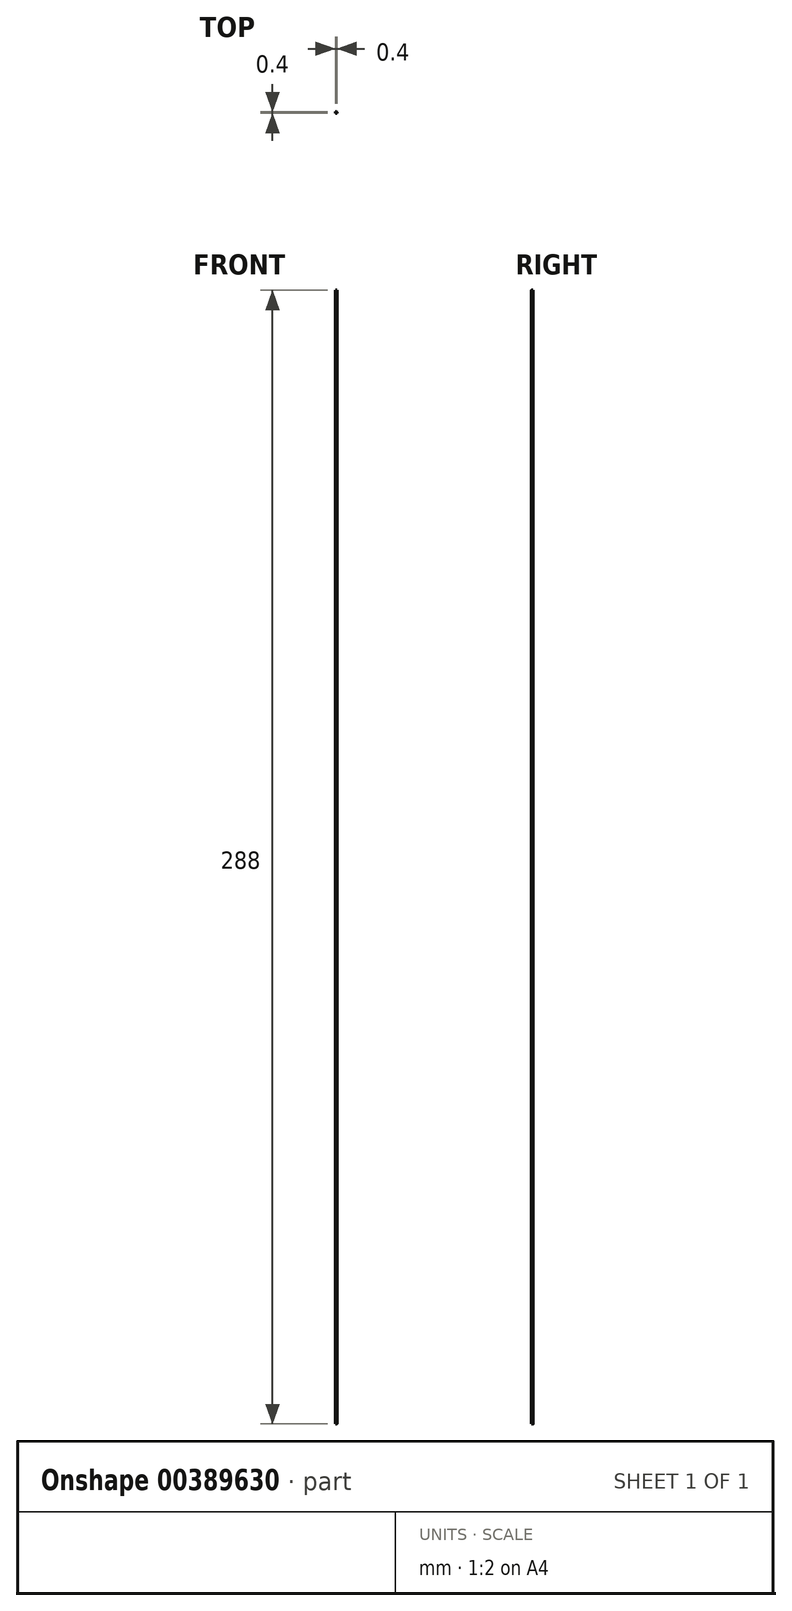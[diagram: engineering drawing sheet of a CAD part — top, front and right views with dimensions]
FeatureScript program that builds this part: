
annotation { "Feature Type Name" : "Feature", "Feature Type Description" : "" }
export const myFeature = defineFeature(function(context is Context, id is Id, definition is map)
    precondition{}
    {
        {
            var Q0;
            Q0=qCreatedBy(makeId("Top.planeOp"),FACE);
            var sketch = newSketch(context, id + "F0", { "sketchPlane" : qUnion([Q0])});
            skCircle(sketch, "E0", {"center": v(0, 0) * mm, "radius": 0.2 * mm});
            skSolve(sketch);
        }
        {
            var Q0;
            Q0=qSketchRegion(id+"F0",true);
            extrude(context, id + "F1", {"entities" : qUnion([Q0]), "depth" : 288 * mm});
        }
    });
